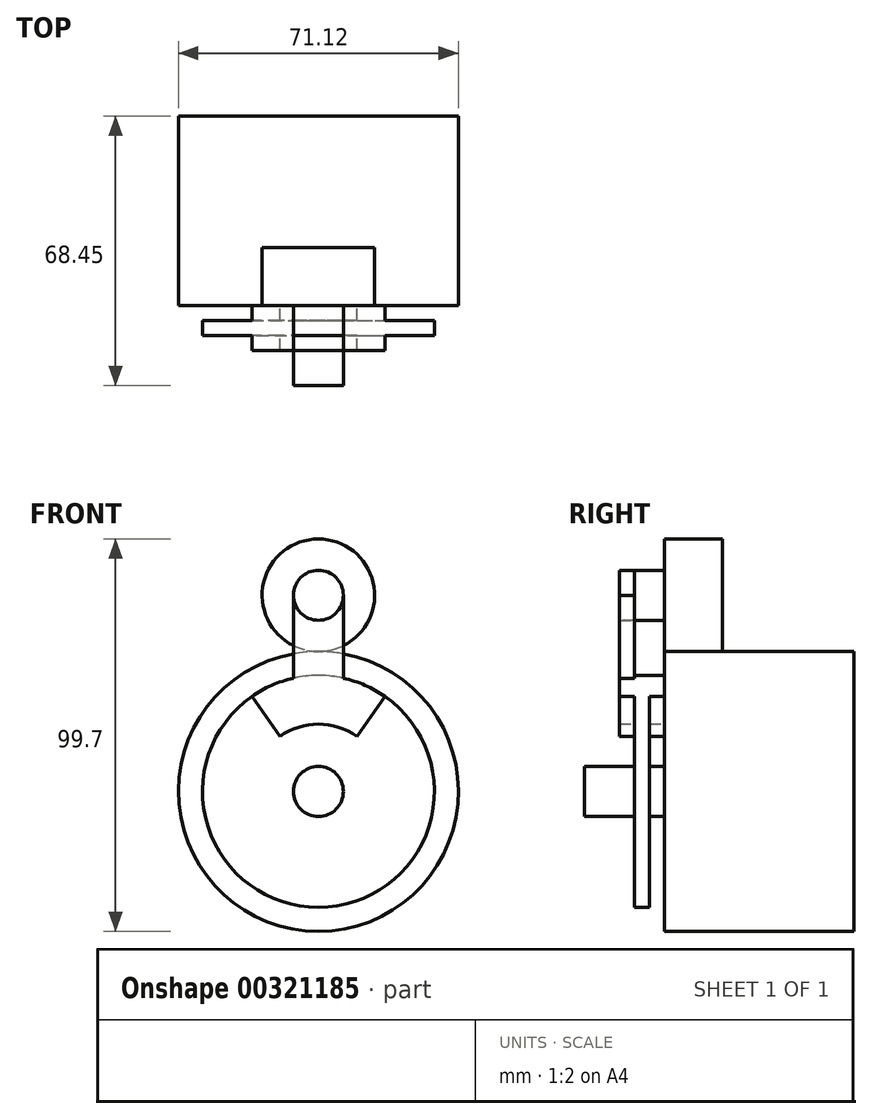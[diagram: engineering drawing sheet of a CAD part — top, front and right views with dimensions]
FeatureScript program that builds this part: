
annotation { "Feature Type Name" : "Feature", "Feature Type Description" : "" }
export const myFeature = defineFeature(function(context is Context, id is Id, definition is map)
    precondition{}
    {
        {
            var Q0;
            Q0=qCreatedBy(makeId("Front.planeOp"),FACE);
            var sketch = newSketch(context, id + "F0", { "sketchPlane" : qUnion([Q0])});
            skCircle(sketch, "E0", {"center": v(0, 0) * mm, "radius": 35.56 * mm});
            skSolve(sketch);
        }
        {
            var Q0;
            Q0=makeQuery(id+"F0.imprint","IMPRINT",FACE,{"disambiguationData":[TD([[makeQuery(id+"F0.imprint","IMPRINT",EDGE,{"derivedFrom":sQuery(id+"F0.wireOp",EDGE,"E0")}),1.0]])]});
            extrude(context, id + "F1", {"entities" : qUnion([Q0]), "depth" : 48.13 * mm});
        }
        {
            var Q0;
            Q0=makeQuery(id+"F1.opExtrude","CAP_FACE",FACE,{"disambiguationData":[OSD([sQuery(id+"F0.wireOp",EDGE,"E0")])],"isStart":false});
            var sketch = newSketch(context, id + "F2", { "sketchPlane" : qUnion([Q0])});
            skCircle(sketch, "E1", {"center": v(0, 49.85) * mm, "radius": 14.29 * mm});
            skSolve(sketch);
        }
        {
            var Q0;
            Q0=makeQuery(id+"F2.imprint","IMPRINT",FACE,{"disambiguationData":[TD([[makeQuery(id+"F2.imprint","IMPRINT",EDGE,{"derivedFrom":sQuery(id+"F2.wireOp",EDGE,"E1")}),1.0]])]});
            extrude(context, id + "F3", {"entities" : qUnion([Q0]), "operationType" : NewBodyOperationType.ADD, "oppositeDirection" : true, "depth" : 14.73 * mm});
        }
        {
            var Q0;
            Q0=makeQuery(id+"F1.opExtrude","CAP_FACE",FACE,{"disambiguationData":[OSD([sQuery(id+"F0.wireOp",EDGE,"E0")])],"isStart":false});
            var sketch = newSketch(context, id + "F4", { "sketchPlane" : qUnion([Q0])});
            skCircle(sketch, "E2", {"center": v(0, 0) * mm, "radius": 6.35 * mm});
            skSolve(sketch);
        }
        {
            var Q0;
            Q0 = qSketchRegion(id + "F4", true);
            extrude(context, id + "F5", {"entities" : qUnion([Q0]), "operationType" : NewBodyOperationType.ADD, "depth" : 3.8 * mm});
        }
        {
            var Q0;
            Q0=makeQuery(id+"F1.opExtrude","CAP_FACE",FACE,{"disambiguationData":[OSD([sQuery(id+"F0.wireOp",EDGE,"E0")])],"isStart":false});
            var sketch = newSketch(context, id + "F6", { "sketchPlane" : qUnion([Q0])});
            skArc(sketch, "E3", {"start": v(9.8, 14) * mm, "mid": v(0, 17.1) * mm, "end": v(-9.8, 14) * mm});
            skArc(sketch, "E4", {"start": v(16.9, 24.14) * mm, "mid": v(0, 29.46) * mm, "end": v(-16.9, 24.14) * mm});
            skLineSegment(sketch, "E5", {"start": v(0, 0) * mm, "end": v(0, 29.46) * mm, "construction": true});
            skLineSegment(sketch, "E6", {"start": v(-9.8, 14) * mm, "end": v(-16.9, 24.14) * mm});
            skLineSegment(sketch, "E7", {"start": v(9.8, 14) * mm, "end": v(16.9, 24.14) * mm});
            skSolve(sketch);
        }
        {
            var Q0;
            Q0=makeQuery(id+"F6.imprint","IMPRINT",FACE,{"disambiguationData":[TD([[makeQuery(id+"F6.imprint","IMPRINT",EDGE,{"derivedFrom":sQuery(id+"F6.wireOp",EDGE,"E3")}),-1.0]])]});
            extrude(context, id + "F7", {"entities" : qUnion([Q0]), "operationType" : NewBodyOperationType.ADD, "depth" : 3.8 * mm});
        }
        {
            var Q0;
            Q0=makeQuery(id+"F3.opExtrude","CAP_FACE",FACE,{"disambiguationData":[OSD([sQuery(id+"F2.wireOp",EDGE,"E1")])],"isStart":true});
            var sketch = newSketch(context, id + "F8", { "sketchPlane" : qUnion([Q0])});
            skCircle(sketch, "E8", {"center": v(0, 49.85) * mm, "radius": 6.35 * mm});
            skSolve(sketch);
        }
        {
            var Q0;
            Q0=makeQuery(id+"F8.imprint","IMPRINT",FACE,{"disambiguationData":[TD([[makeQuery(id+"F8.imprint","IMPRINT",EDGE,{"derivedFrom":sQuery(id+"F8.wireOp",EDGE,"E8")}),1.0]])]});
            extrude(context, id + "F9", {"entities" : qUnion([Q0]), "operationType" : NewBodyOperationType.ADD, "depth" : 7.62 * mm});
        }
        {
            var Q0;
            Q0=makeQuery(id+"F5.opExtrude","CAP_FACE",FACE,{"disambiguationData":[OSD([sQuery(id+"F4.wireOp",EDGE,"E2")])],"isStart":false});
            var sketch = newSketch(context, id + "F10", { "sketchPlane" : qUnion([Q0])});
            skCircle(sketch, "E9", {"center": v(0, 0) * mm, "radius": 29.46 * mm});
            skSolve(sketch);
        }
        {
            var Q0;
            Q0 = qSketchRegion(id + "F10", true);
            extrude(context, id + "F11", {"entities" : qUnion([Q0]), "operationType" : NewBodyOperationType.ADD, "depth" : 3.8 * mm});
        }
        {
            var Q0;
            Q0=makeQuery(id+"F11.opExtrude","CAP_FACE",FACE,{"disambiguationData":[OSD([sQuery(id+"F10.wireOp",EDGE,"E9")])],"isStart":false});
            var sketch = newSketch(context, id + "F12", { "sketchPlane" : qUnion([Q0])});
            skCircle(sketch, "E10", {"center": v(0, 0) * mm, "radius": 6.35 * mm});
            skSolve(sketch);
        }
        {
            var Q0;
            Q0 = qSketchRegion(id + "F12", true);
            extrude(context, id + "F13", {"entities" : qUnion([Q0]), "operationType" : NewBodyOperationType.ADD, "depth" : 12.7 * mm});
        }
        {
            var Q0;
            Q0=makeQuery(id+"F11.opExtrude","CAP_FACE",FACE,{"disambiguationData":[OSD([sQuery(id+"F10.wireOp",EDGE,"E9")])],"isStart":false});
            var sketch = newSketch(context, id + "F14", { "sketchPlane" : qUnion([Q0])});
            skArc(sketch, "E11", {"start": v(9.8, 14) * mm, "mid": v(0, 17.1) * mm, "end": v(-9.8, 14) * mm});
            skArc(sketch, "E12", {"start": v(16.9, 24.14) * mm, "mid": v(0, 29.46) * mm, "end": v(-16.9, 24.14) * mm});
            skLineSegment(sketch, "E13", {"start": v(0, 0) * mm, "end": v(0, 29.46) * mm, "construction": true});
            skLineSegment(sketch, "E14", {"start": v(-9.8, 14) * mm, "end": v(-16.9, 24.14) * mm});
            skLineSegment(sketch, "E15", {"start": v(9.8, 14) * mm, "end": v(16.9, 24.14) * mm});
            skSolve(sketch);
        }
        {
            var Q0;
            Q0=makeQuery(id+"F14.imprint","IMPRINT",FACE,{"disambiguationData":[TD([[makeQuery(id+"F14.imprint","IMPRINT",EDGE,{"derivedFrom":sQuery(id+"F14.wireOp",EDGE,"E11")}),-1.0]])]});
            extrude(context, id + "F15", {"entities" : qUnion([Q0]), "operationType" : NewBodyOperationType.ADD, "depth" : 3.8 * mm});
        }
        {
            var Q0;
            Q0=makeQuery(id+"F9.opExtrude","CAP_FACE",FACE,{"disambiguationData":[OSD([sQuery(id+"F8.wireOp",EDGE,"E8")])],"isStart":false});
            var sketch = newSketch(context, id + "F16", { "sketchPlane" : qUnion([Q0])});
            skLineSegment(sketch, "E16", {"start": v(0, 0) * mm, "end": v(0, 49.85) * mm, "construction": true});
            skLineSegment(sketch, "E17", {"start": v(0, 0) * mm, "end": v(0, 23.27) * mm, "construction": true});
            skLineSegment(sketch, "E18", {"start": v(0, 23.27) * mm, "end": v(0, 30.66) * mm, "construction": true});
            skLineSegment(sketch, "E19.bottom", {"start": v(-6.35, 49.85) * mm, "end": v(6.35, 49.85) * mm});
            skLineSegment(sketch, "E19.top", {"start": v(-6.35, 17.12) * mm, "end": v(6.35, 17.12) * mm});
            skLineSegment(sketch, "E19.left", {"start": v(-6.35, 49.85) * mm, "end": v(-6.35, 17.12) * mm});
            skLineSegment(sketch, "E19.right", {"start": v(6.35, 49.85) * mm, "end": v(6.35, 17.12) * mm});
            skSolve(sketch);
        }
        {
            var Q0;
            Q0=makeQuery(id+"F16.imprint","IMPRINT",FACE,{"disambiguationData":[TD([[makeQuery(id+"F16.imprint","IMPRINT",EDGE,{"derivedFrom":sQuery(id+"F16.wireOp",EDGE,"E19.top")}),1.0]])]});
            extrude(context, id + "F17", {"entities" : qUnion([Q0]), "operationType" : NewBodyOperationType.ADD, "depth" : 3.8 * mm});
        }
        {
            var Q0;
            Q0=makeQuery(id+"F17.boolean.opBoolean","MERGE",FACE,{"derivedFrom":[makeQuery(id+"F15.opExtrude","CAP_FACE",FACE,{"disambiguationData":[OSD([sQuery(id+"F14.wireOp",EDGE,"E11"),sQuery(id+"F14.wireOp",EDGE,"E12"),sQuery(id+"F14.wireOp",EDGE,"E14"),sQuery(id+"F14.wireOp",EDGE,"E15")])],"isStart":false}),makeQuery(id+"F17.opExtrude","CAP_FACE",FACE,{"disambiguationData":[OSD([sQuery(id+"F8.wireOp",EDGE,"E8"),sQuery(id+"F16.wireOp",EDGE,"E19.top"),sQuery(id+"F16.wireOp",EDGE,"E19.left"),sQuery(id+"F16.wireOp",EDGE,"E19.right")])],"isStart":false})]});
            var sketch = newSketch(context, id + "F18", { "sketchPlane" : qUnion([Q0])});
            skCircle(sketch, "E20", {"center": v(0, 49.85) * mm, "radius": 6.35 * mm});
            skSolve(sketch);
        }
        {
            var Q0;
            {var subQ0=sQuery(id+"F18.wireOp",EDGE,"E20");var subQ1=makeQuery(id+"F18.imprint","INTERSECT",VERTEX,{"derivedFrom":[makeQuery(id+"F17.opExtrude","CAP_EDGE",EDGE,{"disambiguationData":[OSD([sQuery(id+"F16.wireOp",EDGE,"E19.left")])],"isStart":false}),subQ0]});Q0=makeQuery(id+"F18.imprint","IMPRINT",FACE,{"disambiguationData":[TD([[makeQuery(id+"F18.imprint","IMPRINT",EDGE,{"disambiguationData":[TD([[subQ1,1.0]])],"derivedFrom":subQ0}),1.0]])]});}
            extrude(context, id + "F19", {"entities" : qUnion([Q0]), "oppositeDirection" : true, "depth" : 3.8 * mm});
        }
    });
